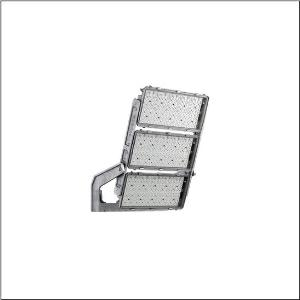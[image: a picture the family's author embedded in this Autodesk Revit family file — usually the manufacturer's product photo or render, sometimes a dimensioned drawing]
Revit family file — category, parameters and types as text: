
# Revit family: floodlight_fl_11_maxi_pro_remote___pl43_5xa779425a01aa_2185
name_source: partatom
category: Lighting Fixtures
units: mm (PartAtom-declared; Revit-internal decimal feet)

## family parameters
Cut with Voids When Loaded = No
Host = Face
Light Source = No
Part Type = Normal
Room Calculation Point = No
Round Connector Dimension = Use Diameter
Shared = No

## types (1)
- --- (1 x LED, 162210 lm, 1334.7 W, 3000K)
    Apparent Load = 1335 VA
    CIE Flux Codes = 25 74 99 100 100
    Color Rendering = 70
    Color Temperature = 3000K
    Default Elevation = 1800 mm
    Description = Floodlight FL 11  maxi  pro Remote floodlight; light control with lens of PMMA; cover panel of toughened safety glass, transparent; light distribution: PL43, asymmetric direct distribution, LEDcolour temperature: 3000K, rated luminous flux: 162.210lm, colour rendering: CRI > 70, light colour: 730; luminous efficacy: 122lm/W; brightness control: DALI 2 (1 DALI address); with terminal, 8-pole, max. 2.5mm², mains connection: 220..240V/380..400V AC, 50/60Hz, surge voltage resistance: line to ground: 10kV, ECG replaceable separately, LED unit replaceable without ESD environment, dustproof LED module, dimming range 10..100%, no afterglow with DALI off / DMX off command; 1335W floodlight with 2x LED unit of diecast aluminium, coated grey; length: 713mm / width: 651mm / height: 338mm; mounting bracket, of diecast aluminium, uncoated, natural, equipment: Power, protection rating (complete): IP66; insulation class (complete): insulation class I (protective earthing); certification: CE, ENEC, VDE; ball protection: ball impact resistance with accessories, impact resistance: IK07; rated ambient temperature 10°C, only for outdoor installations, permissible operating ambient temperature: -40..+30°C, permissible storage temperature: -40..+85°C; packaging unit: 1 piece

Light Distribution: PL43
    Height = 320 mm
    Lamp = 1 x LED
    Lamp Light Flux = 162210 lm
    Lamp Power = 1334.7 W
    Lamp count = 1
    Length = 1002 mm
    Luminous efficacy = 122 lm/W
    Manufacturer = Siteco
    ModVariant = No
    Model = 5XA779425A01AA
    Mounting Place = Ceiling
    Mounting Type = Surface mounted
    Number of Poles = 1
    OnlyDefault = Yes
    Power Factor = 1
    Product Name = Floodlight FL 11 maxi pro Remote | PL43
    Product group = floodlight | ceiling mounted
    ProductGroupID = 302
    Protection Class = Protection class I
    Protection Degree = IP 66
    RLX_Detail_Level = 1
    RLX_Emergency_Light_Flux = 0 lm
    RLX_Emergency_Type = 0
    RLX_Emergency_Type_DB = No
    RlxData = <blob elided: 52501 chars, md5=ae6fba03>
    Socket = socket
    Standby Power = 0 W
    System Light Flux = 162210 lm
    System Power = 1335 W
    Type Comments = factory setting: luminous flux: 100 % | dim-lin: 254 | 920 mA
    Type Image = l_1006784.jpg
    URL = http://relux.com
    VarID = @adj_026721
    Voltage = 0 V
    Weight = 0.00 kg
    Width = 655 mm

## geometry (parser evidence)
native form markers: Blend x4, Sweep x12
no freeform markers — native parametric forms only
